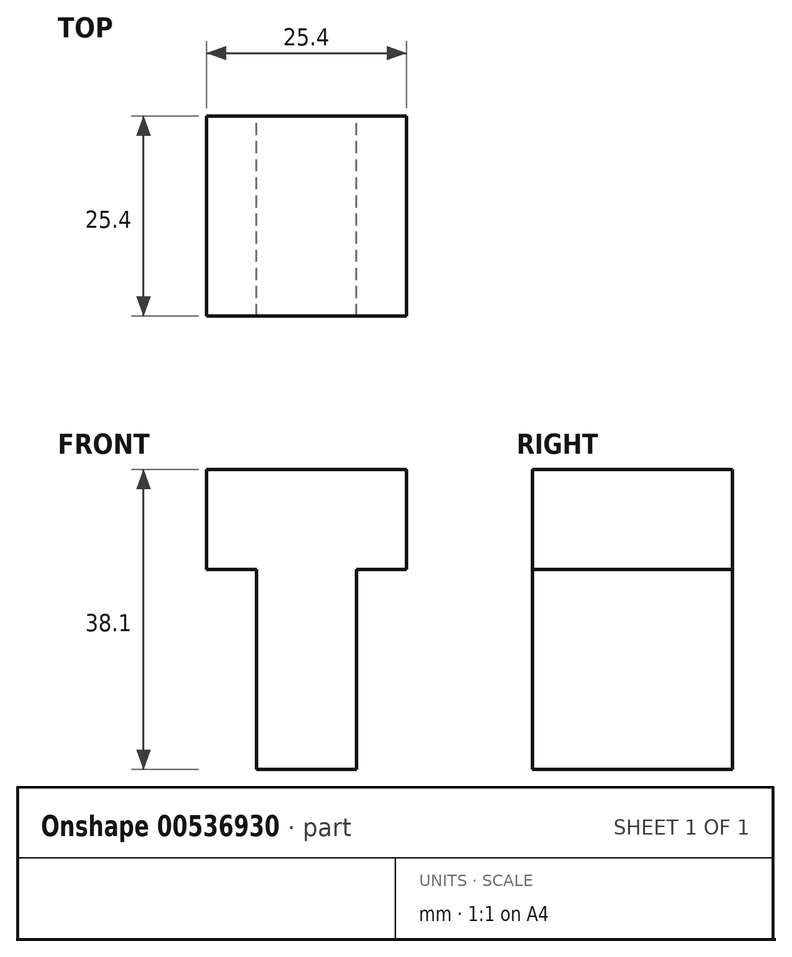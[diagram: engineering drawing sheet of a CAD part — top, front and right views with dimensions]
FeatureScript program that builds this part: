
annotation { "Feature Type Name" : "Feature", "Feature Type Description" : "" }
export const myFeature = defineFeature(function(context is Context, id is Id, definition is map)
    precondition{}
    {
        {
            var Q0;
            Q0=qCreatedBy(makeId("Front.planeOp"),FACE);
            var sketch = newSketch(context, id + "F0", { "sketchPlane" : qUnion([Q0])});
            skLineSegment(sketch, "E0", {"start": v(-27.87, 38.1) * mm, "end": v(-2.47, 38.1) * mm});
            skLineSegment(sketch, "E1", {"start": v(-2.47, 38.1) * mm, "end": v(-2.47, 25.4) * mm});
            skLineSegment(sketch, "E2", {"start": v(-2.47, 25.4) * mm, "end": v(-8.82, 25.4) * mm});
            skLineSegment(sketch, "E3", {"start": v(-8.82, 25.4) * mm, "end": v(-8.82, 0) * mm});
            skLineSegment(sketch, "E4", {"start": v(-8.82, 0) * mm, "end": v(-21.52, 0) * mm});
            skLineSegment(sketch, "E5", {"start": v(-21.52, 0) * mm, "end": v(-21.52, 25.4) * mm});
            skLineSegment(sketch, "E6", {"start": v(-21.52, 25.4) * mm, "end": v(-27.87, 25.4) * mm});
            skLineSegment(sketch, "E7", {"start": v(-27.87, 25.4) * mm, "end": v(-27.87, 38.1) * mm});
            skSolve(sketch);
        }
        {
            var Q0;
            Q0 = qSketchRegion(id + "F0", true);
            extrude(context, id + "F1", {"entities" : qUnion([Q0]), "depth" : 25.4 * mm, "offsetDistance" : 25.4 * mm});
        }
    });
